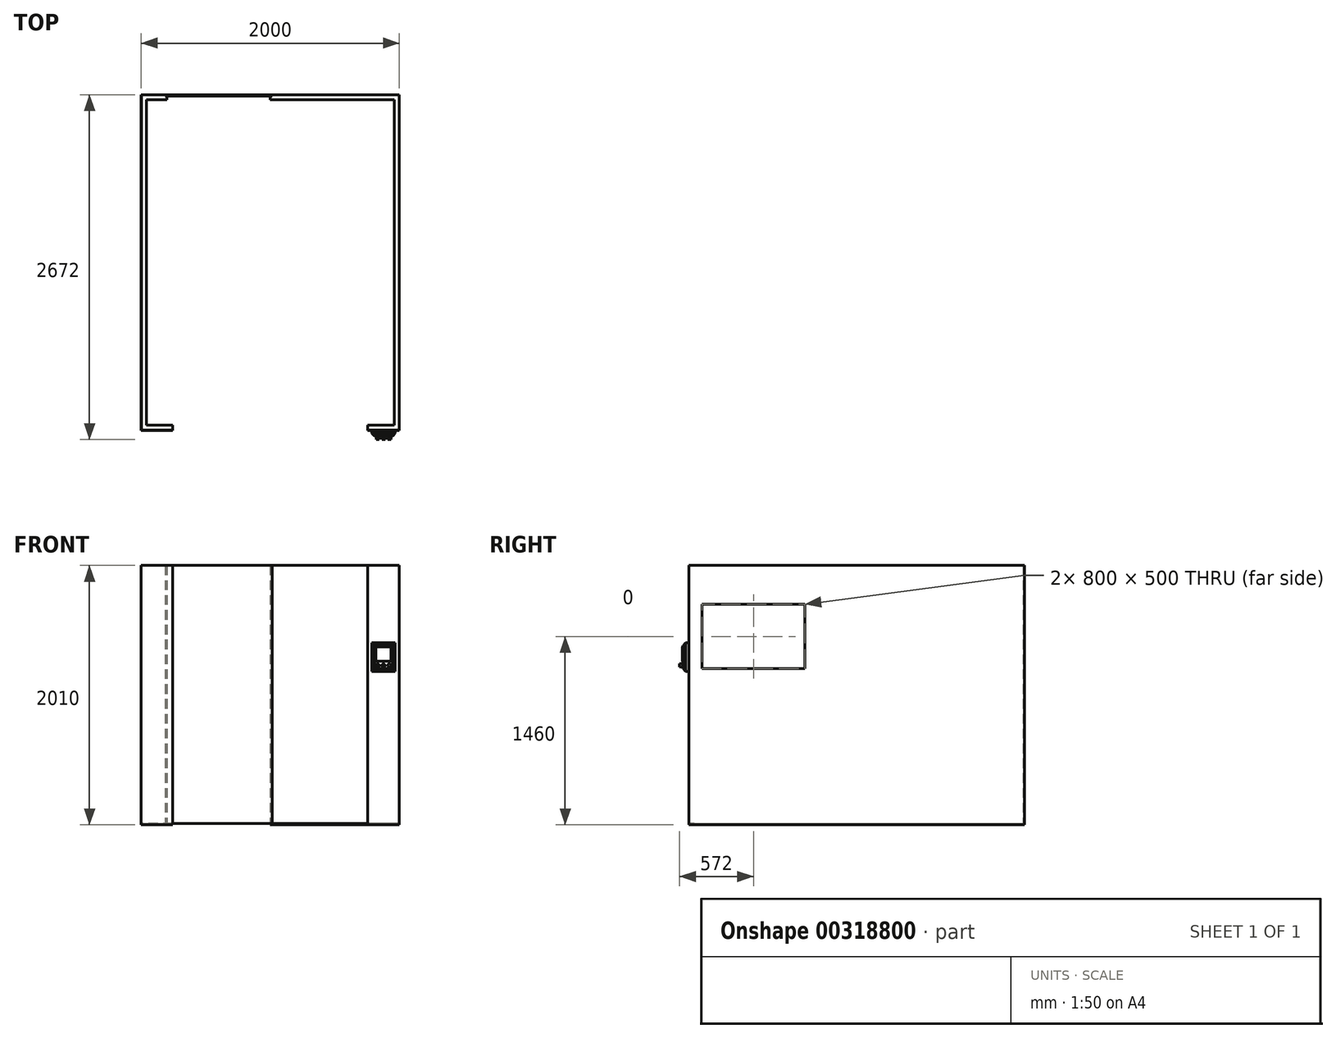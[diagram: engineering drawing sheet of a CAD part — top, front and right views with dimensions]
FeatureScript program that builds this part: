
annotation { "Feature Type Name" : "Feature", "Feature Type Description" : "" }
export const myFeature = defineFeature(function(context is Context, id is Id, definition is map)
    precondition{}
    {
        {
            var Q0;
            Q0=qCreatedBy(makeId("Top.planeOp"),FACE);
            var sketch = newSketch(context, id + "F0", { "sketchPlane" : qUnion([Q0])});
            skLineSegment(sketch, "E0", {"start": v(0, 0) * mm, "end": v(-755, 0) * mm, "construction": true});
            skLineSegment(sketch, "E1.MirrorCS", {"start": v(0, 0) * mm, "end": v(755, 0) * mm, "construction": true});
            skLineSegment(sketch, "E2", {"start": v(-755, 0) * mm, "end": v(-755, -20) * mm});
            skLineSegment(sketch, "E3", {"start": v(-755, -20) * mm, "end": v(-1000, -20) * mm});
            skLineSegment(sketch, "E4", {"start": v(-1000, -20) * mm, "end": v(-1000, 0) * mm});
            skLineSegment(sketch, "E5.MirrorCS", {"start": v(-755, 0) * mm, "end": v(-755, 20) * mm});
            skLineSegment(sketch, "E6.MirrorCS", {"start": v(-1000, 20) * mm, "end": v(-1000, 0) * mm});
            skLineSegment(sketch, "E7.MirrorCS", {"start": v(-755, 20) * mm, "end": v(-960, 20) * mm});
            skLineSegment(sketch, "E8.MirrorCS", {"start": v(755, 0) * mm, "end": v(755, -20) * mm});
            skLineSegment(sketch, "E9.MirrorCS", {"start": v(755, 0) * mm, "end": v(755, 20) * mm});
            skLineSegment(sketch, "E10.MirrorCS", {"start": v(1000, 20) * mm, "end": v(1000, 0) * mm});
            skLineSegment(sketch, "E11.MirrorCS", {"start": v(1000, -20) * mm, "end": v(1000, 0) * mm});
            skLineSegment(sketch, "E12.MirrorCS", {"start": v(755, 20) * mm, "end": v(960, 20) * mm});
            skLineSegment(sketch, "E13.MirrorCS", {"start": v(755, -20) * mm, "end": v(1000, -20) * mm});
            skLineSegment(sketch, "E14.left", {"start": v(-1000, 20) * mm, "end": v(-1000, 2540) * mm});
            skLineSegment(sketch, "E14.right", {"start": v(-960, 20) * mm, "end": v(-960, 2540) * mm});
            skLineSegment(sketch, "E15.MirrorCS", {"start": v(1000, 20) * mm, "end": v(1000, 2540) * mm});
            skLineSegment(sketch, "E16.MirrorCS", {"start": v(960, 20) * mm, "end": v(960, 2540) * mm});
            skLineSegment(sketch, "E17.bottom", {"start": v(-960, 2540) * mm, "end": v(-800, 2540) * mm});
            skLineSegment(sketch, "E17.top", {"start": v(-1000, 2580) * mm, "end": v(-800, 2580) * mm});
            skLineSegment(sketch, "E17.left", {"start": v(-1000, 2540) * mm, "end": v(-1000, 2580) * mm});
            skLineSegment(sketch, "E17.right", {"start": v(-800, 2540) * mm, "end": v(-800, 2580) * mm});
            skLineSegment(sketch, "E18.bottom", {"start": v(960, 2540) * mm, "end": v(0, 2540) * mm});
            skLineSegment(sketch, "E18.top", {"start": v(1000, 2580) * mm, "end": v(0, 2580) * mm});
            skLineSegment(sketch, "E18.left", {"start": v(1000, 2540) * mm, "end": v(1000, 2580) * mm});
            skLineSegment(sketch, "E18.right", {"start": v(0, 2540) * mm, "end": v(0, 2580) * mm});
            skSolve(sketch);
        }
        {
            var Q0;
            Q0=qSketchRegion(id+"F0",true);
            extrude(context, id + "F1", {"entities" : qUnion([Q0]), "depth" : 10 * mm});
        }
        {
            var Q0;
            Q0=makeQuery(id+"F1.opExtrude","CAP_FACE",FACE,{"disambiguationData":[OSD([sQuery(id+"F0.wireOp",EDGE,"E2"),sQuery(id+"F0.wireOp",EDGE,"E3"),sQuery(id+"F0.wireOp",EDGE,"E4"),sQuery(id+"F0.wireOp",EDGE,"E5.MirrorCS"),sQuery(id+"F0.wireOp",EDGE,"E6.MirrorCS"),sQuery(id+"F0.wireOp",EDGE,"E7.MirrorCS"),sQuery(id+"F0.wireOp",EDGE,"E14.left"),sQuery(id+"F0.wireOp",EDGE,"E14.right"),sQuery(id+"F0.wireOp",EDGE,"E17.bottom"),sQuery(id+"F0.wireOp",EDGE,"E17.top"),sQuery(id+"F0.wireOp",EDGE,"E17.left"),sQuery(id+"F0.wireOp",EDGE,"E17.right")])],"isStart":false});
            var sketch = newSketch(context, id + "F2", { "sketchPlane" : qUnion([Q0])});
            skLineSegment(sketch, "E19", {"start": v(-800, 2580) * mm, "end": v(-1000, 2580) * mm});
            skLineSegment(sketch, "E20", {"start": v(-1000, 2580) * mm, "end": v(-1000, -20) * mm});
            skLineSegment(sketch, "E21", {"start": v(-1000, -20) * mm, "end": v(-755, -20) * mm});
            skLineSegment(sketch, "E22", {"start": v(-755, -20) * mm, "end": v(-755, -18) * mm});
            skLineSegment(sketch, "E23", {"start": v(-755, -18) * mm, "end": v(-998, -18) * mm});
            skLineSegment(sketch, "E24", {"start": v(-998, -18) * mm, "end": v(-998, 2578) * mm});
            skLineSegment(sketch, "E25", {"start": v(-998, 2578) * mm, "end": v(-800, 2578) * mm});
            skLineSegment(sketch, "E26", {"start": v(-800, 2578) * mm, "end": v(-800, 2580) * mm});
            skSolve(sketch);
        }
        {
            var Q0;
            Q0=qSketchRegion(id+"F2",true);
            extrude(context, id + "F3", {"entities" : qUnion([Q0]), "operationType" : NewBodyOperationType.ADD, "depth" : 2000 * mm});
        }
        {
            var Q0;
            Q0=makeQuery(id+"F1.opExtrude","CAP_FACE",FACE,{"disambiguationData":[OSD([sQuery(id+"F0.wireOp",EDGE,"E8.MirrorCS"),sQuery(id+"F0.wireOp",EDGE,"E9.MirrorCS"),sQuery(id+"F0.wireOp",EDGE,"E11.MirrorCS"),sQuery(id+"F0.wireOp",EDGE,"E12.MirrorCS"),sQuery(id+"F0.wireOp",EDGE,"E13.MirrorCS"),sQuery(id+"F0.wireOp",EDGE,"E10.MirrorCS"),sQuery(id+"F0.wireOp",EDGE,"E15.MirrorCS"),sQuery(id+"F0.wireOp",EDGE,"E16.MirrorCS"),sQuery(id+"F0.wireOp",EDGE,"E18.bottom"),sQuery(id+"F0.wireOp",EDGE,"E18.top"),sQuery(id+"F0.wireOp",EDGE,"E18.left"),sQuery(id+"F0.wireOp",EDGE,"E18.right")])],"isStart":false});
            var sketch = newSketch(context, id + "F4", { "sketchPlane" : qUnion([Q0])});
            skLineSegment(sketch, "E27", {"start": v(0, 2580) * mm, "end": v(1000, 2580) * mm});
            skLineSegment(sketch, "E28", {"start": v(1000, 2580) * mm, "end": v(1000, -20) * mm});
            skLineSegment(sketch, "E29", {"start": v(1000, -20) * mm, "end": v(755, -20) * mm});
            skLineSegment(sketch, "E30", {"start": v(755, -20) * mm, "end": v(755, -18) * mm});
            skLineSegment(sketch, "E31", {"start": v(755, -18) * mm, "end": v(998, -18) * mm});
            skLineSegment(sketch, "E32", {"start": v(998, -18) * mm, "end": v(998, 2578) * mm});
            skLineSegment(sketch, "E33", {"start": v(998, 2578) * mm, "end": v(0, 2578) * mm});
            skLineSegment(sketch, "E34", {"start": v(0, 2578) * mm, "end": v(0, 2580) * mm});
            skSolve(sketch);
        }
        {
            var Q0;
            Q0=qSketchRegion(id+"F4",true);
            extrude(context, id + "F5", {"entities" : qUnion([Q0]), "operationType" : NewBodyOperationType.ADD, "depth" : 2000 * mm});
        }
        {
            var Q0;
            Q0=makeQuery(id+"F5.boolean.opBoolean","MERGE",FACE,{"derivedFrom":[makeQuery(id+"F1.opExtrude","SWEPT_FACE",FACE,{"disambiguationData":[OSD([sQuery(id+"F0.wireOp",EDGE,"E18.top")])]}),makeQuery(id+"F5.opExtrude","SWEPT_FACE",FACE,{"disambiguationData":[OSD([sQuery(id+"F4.wireOp",EDGE,"E27")])]})]});
            var sketch = newSketch(context, id + "F6", { "sketchPlane" : qUnion([Q0])});
            skLineSegment(sketch, "E35.bottom", {"start": v(-15, 2010) * mm, "end": v(815, 2010) * mm});
            skLineSegment(sketch, "E35.top", {"start": v(-15, 10) * mm, "end": v(815, 10) * mm});
            skLineSegment(sketch, "E35.left", {"start": v(-15, 2010) * mm, "end": v(-15, 10) * mm});
            skLineSegment(sketch, "E35.right", {"start": v(815, 2010) * mm, "end": v(815, 10) * mm});
            skSolve(sketch);
        }
        {
            var Q0;
            Q0=qSketchRegion(id+"F6",true);
            extrude(context, id + "F7", {"entities" : qUnion([Q0]), "oppositeDirection" : true, "depth" : 10 * mm});
        }
        {
            var Q0;
            Q0=makeQuery(id+"F5.boolean.opBoolean","MERGE",FACE,{"derivedFrom":[makeQuery(id+"F1.opExtrude","SWEPT_FACE",FACE,{"disambiguationData":[OSD([sQuery(id+"F0.wireOp",EDGE,"E11.MirrorCS"),sQuery(id+"F0.wireOp",EDGE,"E10.MirrorCS"),sQuery(id+"F0.wireOp",EDGE,"E15.MirrorCS"),sQuery(id+"F0.wireOp",EDGE,"E18.left")])]}),makeQuery(id+"F5.opExtrude","SWEPT_FACE",FACE,{"disambiguationData":[OSD([sQuery(id+"F4.wireOp",EDGE,"E28")])]})]});
            var sketch = newSketch(context, id + "F8", { "sketchPlane" : qUnion([Q0])});
            skLineSegment(sketch, "E36.bottom", {"start": v(80, 1710) * mm, "end": v(880, 1710) * mm});
            skLineSegment(sketch, "E36.top", {"start": v(80, 1210) * mm, "end": v(880, 1210) * mm});
            skLineSegment(sketch, "E36.left", {"start": v(80, 1710) * mm, "end": v(80, 1210) * mm});
            skLineSegment(sketch, "E36.right", {"start": v(880, 1710) * mm, "end": v(880, 1210) * mm});
            skSolve(sketch);
        }
        {
            var Q0;
            Q0=qSketchRegion(id+"F8",true);
            extrude(context, id + "F9", {"entities" : qUnion([Q0]), "operationType" : NewBodyOperationType.REMOVE, "oppositeDirection" : true, "depth" : 5 * mm});
        }
        {
            var Q0;
            Q0=makeQuery(id+"F3.boolean.opBoolean","MERGE",FACE,{"derivedFrom":[makeQuery(id+"F1.opExtrude","SWEPT_FACE",FACE,{"disambiguationData":[OSD([sQuery(id+"F0.wireOp",EDGE,"E4"),sQuery(id+"F0.wireOp",EDGE,"E6.MirrorCS"),sQuery(id+"F0.wireOp",EDGE,"E14.left"),sQuery(id+"F0.wireOp",EDGE,"E17.left")])]}),makeQuery(id+"F3.opExtrude","SWEPT_FACE",FACE,{"disambiguationData":[OSD([sQuery(id+"F2.wireOp",EDGE,"E20")])]})]});
            var sketch = newSketch(context, id + "F10", { "sketchPlane" : qUnion([Q0])});
            skLineSegment(sketch, "E37.bottom", {"start": v(-880, 1710) * mm, "end": v(-80, 1710) * mm});
            skLineSegment(sketch, "E37.top", {"start": v(-880, 1210) * mm, "end": v(-80, 1210) * mm});
            skLineSegment(sketch, "E37.left", {"start": v(-880, 1710) * mm, "end": v(-880, 1210) * mm});
            skLineSegment(sketch, "E37.right", {"start": v(-80, 1710) * mm, "end": v(-80, 1210) * mm});
            skSolve(sketch);
        }
        {
            var Q0;
            Q0=qSketchRegion(id+"F10",true);
            extrude(context, id + "F11", {"entities" : qUnion([Q0]), "operationType" : NewBodyOperationType.REMOVE, "oppositeDirection" : true, "depth" : 5 * mm});
        }
        {
            var Q0;
            Q0=makeQuery(id+"F3.boolean.opBoolean","MERGE",FACE,{"derivedFrom":[makeQuery(id+"F1.opExtrude","SWEPT_FACE",FACE,{"disambiguationData":[OSD([sQuery(id+"F0.wireOp",EDGE,"E4"),sQuery(id+"F0.wireOp",EDGE,"E6.MirrorCS"),sQuery(id+"F0.wireOp",EDGE,"E14.left"),sQuery(id+"F0.wireOp",EDGE,"E17.left")])]}),makeQuery(id+"F3.opExtrude","SWEPT_FACE",FACE,{"disambiguationData":[OSD([sQuery(id+"F2.wireOp",EDGE,"E20")])]})]});
            var sketch = newSketch(context, id + "F12", { "sketchPlane" : qUnion([Q0])});
            skLineSegment(sketch, "E38.bottom", {"start": v(-880, 1710) * mm, "end": v(-80, 1710) * mm});
            skLineSegment(sketch, "E38.top", {"start": v(-880, 1210) * mm, "end": v(-80, 1210) * mm});
            skLineSegment(sketch, "E38.left", {"start": v(-880, 1710) * mm, "end": v(-880, 1210) * mm});
            skLineSegment(sketch, "E38.right", {"start": v(-80, 1710) * mm, "end": v(-80, 1210) * mm});
            skSolve(sketch);
        }
        {
            var Q0;
            Q0=qSketchRegion(id+"F12",true);
            extrude(context, id + "F13", {"entities" : qUnion([Q0]), "oppositeDirection" : true, "depth" : 2 * mm});
        }
        {
            var Q0;
            Q0=makeQuery(id+"F5.boolean.opBoolean","MERGE",FACE,{"derivedFrom":[makeQuery(id+"F1.opExtrude","SWEPT_FACE",FACE,{"disambiguationData":[OSD([sQuery(id+"F0.wireOp",EDGE,"E11.MirrorCS"),sQuery(id+"F0.wireOp",EDGE,"E10.MirrorCS"),sQuery(id+"F0.wireOp",EDGE,"E15.MirrorCS"),sQuery(id+"F0.wireOp",EDGE,"E18.left")])]}),makeQuery(id+"F5.opExtrude","SWEPT_FACE",FACE,{"disambiguationData":[OSD([sQuery(id+"F4.wireOp",EDGE,"E28")])]})]});
            var sketch = newSketch(context, id + "F14", { "sketchPlane" : qUnion([Q0])});
            skLineSegment(sketch, "E39.bottom", {"start": v(80, 1710) * mm, "end": v(880, 1710) * mm});
            skLineSegment(sketch, "E39.top", {"start": v(80, 1210) * mm, "end": v(880, 1210) * mm});
            skLineSegment(sketch, "E39.left", {"start": v(80, 1710) * mm, "end": v(80, 1210) * mm});
            skLineSegment(sketch, "E39.right", {"start": v(880, 1710) * mm, "end": v(880, 1210) * mm});
            skSolve(sketch);
        }
        {
            var Q0;
            Q0=qSketchRegion(id+"F14",true);
            extrude(context, id + "F15", {"entities" : qUnion([Q0]), "oppositeDirection" : true, "depth" : 2 * mm});
        }
        {
            var Q0;
            Q0=makeQuery(id+"F3.opExtrude","SWEPT_FACE",FACE,{"disambiguationData":[OSD([sQuery(id+"F2.wireOp",EDGE,"E25")])]});
            var sketch = newSketch(context, id + "F16", { "sketchPlane" : qUnion([Q0])});
            skLineSegment(sketch, "E40", {"start": v(-800, 10) * mm, "end": v(-815, 10) * mm});
            skPoint(sketch, "E41", {"position": v(-815, 10) * mm});
            skSolve(sketch);
        }
        {
            var Q0;
            Q0=makeQuery(id+"F5.boolean.opBoolean","MERGE",FACE,{"derivedFrom":[makeQuery(id+"F1.opExtrude","SWEPT_FACE",FACE,{"disambiguationData":[OSD([sQuery(id+"F0.wireOp",EDGE,"E13.MirrorCS")])]}),makeQuery(id+"F5.opExtrude","SWEPT_FACE",FACE,{"disambiguationData":[OSD([sQuery(id+"F4.wireOp",EDGE,"E29")])]})]});
            var sketch = newSketch(context, id + "F17", { "sketchPlane" : qUnion([Q0])});
            skLineSegment(sketch, "E42.bottom", {"start": v(787.5, 1410) * mm, "end": v(967.5, 1410) * mm});
            skLineSegment(sketch, "E42.top", {"start": v(787.5, 1190) * mm, "end": v(967.5, 1190) * mm});
            skLineSegment(sketch, "E42.left", {"start": v(787.5, 1410) * mm, "end": v(787.5, 1190) * mm});
            skLineSegment(sketch, "E42.right", {"start": v(967.5, 1410) * mm, "end": v(967.5, 1190) * mm});
            skSolve(sketch);
        }
        {
            var Q0;
            Q0=qSketchRegion(id+"F17",true);
            extrude(context, id + "F18", {"entities" : qUnion([Q0]), "depth" : 25 * mm});
        }
        {
            var Q0;
            Q0=makeQuery(id+"F18.opExtrude","CAP_FACE",FACE,{"disambiguationData":[OSD([sQuery(id+"F17.wireOp",EDGE,"E42.bottom"),sQuery(id+"F17.wireOp",EDGE,"E42.top"),sQuery(id+"F17.wireOp",EDGE,"E42.left"),sQuery(id+"F17.wireOp",EDGE,"E42.right")])],"isStart":false});
            cPlane(context, id + "F19", {"entities" : qUnion([Q0]), "cplaneType" : CPlaneType.OFFSET, "offset" : 20 * mm, "width" : 150 * mm, "height" : 150 * mm});
        }
        {
            var Q0;
            Q0=qCreatedBy(id+"F19.planeOp",FACE);
            var sketch = newSketch(context, id + "F20", { "sketchPlane" : qUnion([Q0])});
            skLineSegment(sketch, "E43.0", {"start": v(947.5, 1390) * mm, "end": v(947.5, 1210) * mm});
            skLineSegment(sketch, "E44.0", {"start": v(807.5, 1390) * mm, "end": v(947.5, 1390) * mm});
            skLineSegment(sketch, "E45.0", {"start": v(807.5, 1390) * mm, "end": v(807.5, 1210) * mm});
            skLineSegment(sketch, "E46.0", {"start": v(807.5, 1210) * mm, "end": v(947.5, 1210) * mm});
            skPoint(sketch, "E47.orphan", {"position": v(787.5, 1410) * mm});
            skPoint(sketch, "E48.orphan", {"position": v(787.5, 1190) * mm});
            skPoint(sketch, "E49.0.end.orphan", {"position": v(967.5, 1190) * mm});
            skPoint(sketch, "E50.0.start.orphan", {"position": v(967.5, 1410) * mm});
            skSolve(sketch);
        }
        {
            var Q0;
            Q0=makeQuery(id+"F18.opExtrude","CAP_FACE",FACE,{"disambiguationData":[OSD([sQuery(id+"F17.wireOp",EDGE,"E42.bottom"),sQuery(id+"F17.wireOp",EDGE,"E42.top"),sQuery(id+"F17.wireOp",EDGE,"E42.left"),sQuery(id+"F17.wireOp",EDGE,"E42.right")])],"isStart":false});
            var Q1;
            Q1=makeQuery(id+"F20.imprint","IMPRINT",FACE,{"disambiguationData":[TD([[makeQuery(id+"F20.imprint","IMPRINT",EDGE,{"derivedFrom":sQuery(id+"F20.wireOp",EDGE,"E43.0")}),-1.0]])]});
            var Q2;
            Q2=sQuery(id+"F20.wireOp",EDGE,"E46.0");
            var Q3;
            Q3=sQuery(id+"F20.wireOp",EDGE,"E45.0");
            var Q4;
            Q4=sQuery(id+"F20.wireOp",EDGE,"E44.0");
            var Q5;
            Q5=sQuery(id+"F20.wireOp",EDGE,"E43.0");
            loft(context, id + "F21", {"sheetProfilesArray" : [{ "sheetProfileEntities" : qUnion([Q0]) }, { "sheetProfileEntities" : qUnion([Q1]) }], "guidesArray" : [{ "guideEntities" : qUnion([Q2]), "guideDerivativeType" : LoftGuideDerivativeType.DEFAULT, "guideDerivativeMagnitude" : 1 }, { "guideEntities" : qUnion([Q3]), "guideDerivativeType" : LoftGuideDerivativeType.DEFAULT, "guideDerivativeMagnitude" : 1 }, { "guideEntities" : qUnion([Q4]), "guideDerivativeType" : LoftGuideDerivativeType.DEFAULT, "guideDerivativeMagnitude" : 1 }, { "guideEntities" : qUnion([Q5]), "guideDerivativeType" : LoftGuideDerivativeType.DEFAULT, "guideDerivativeMagnitude" : 1 }]});
        }
        {
            var Q0;
            Q0=makeQuery(id+"F21.opLoft","CAP_FACE",FACE,{"disambiguationData":[OSD([makeQuery(id+"F20.imprint","IMPRINT",FACE,{"disambiguationData":[TD([[makeQuery(id+"F20.imprint","IMPRINT",EDGE,{"derivedFrom":sQuery(id+"F20.wireOp",EDGE,"E43.0")}),-1.0]])]})])],"isStart":true});
            extrude(context, id + "F22", {"entities" : qUnion([Q0]), "endBound" : BoundingType.SYMMETRIC, "depth" : 4 * mm});
        }
        {
            var Q0;
            Q0=makeQuery(id+"F22.opExtrude","CAP_FACE",FACE,{"disambiguationData":[OSD([makeQuery(id+"F20.imprint","IMPRINT",FACE,{"disambiguationData":[TD([[makeQuery(id+"F20.imprint","IMPRINT",EDGE,{"derivedFrom":sQuery(id+"F20.wireOp",EDGE,"E43.0")}),-1.0]])]})])],"isStart":false});
            var sketch = newSketch(context, id + "F23", { "sketchPlane" : qUnion([Q0])});
            skCircle(sketch, "E51", {"center": v(877.5, 1235) * mm, "radius": 12.5 * mm});
            skPoint(sketch, "E51.centerSnap0", {"position": v(877.5, 1210) * mm});
            skCircle(sketch, "E52", {"center": v(832.5, 1235) * mm, "radius": 12.5 * mm});
            skCircle(sketch, "E53", {"center": v(922.5, 1235) * mm, "radius": 12.5 * mm});
            skLineSegment(sketch, "E54", {"start": v(877.5, 1235) * mm, "end": v(832.5, 1235) * mm, "construction": true});
            skLineSegment(sketch, "E55", {"start": v(877.5, 1235) * mm, "end": v(922.5, 1235) * mm, "construction": true});
            skSolve(sketch);
        }
        {
            var Q0;
            Q0=qSketchRegion(id+"F23",true);
            extrude(context, id + "F24", {"entities" : qUnion([Q0]), "depth" : 25 * mm});
        }
        {
            var Q0;
            Q0=makeQuery(id+"F22.opExtrude","CAP_FACE",FACE,{"disambiguationData":[OSD([makeQuery(id+"F20.imprint","IMPRINT",FACE,{"disambiguationData":[TD([[makeQuery(id+"F20.imprint","IMPRINT",EDGE,{"derivedFrom":sQuery(id+"F20.wireOp",EDGE,"E43.0")}),-1.0]])]})])],"isStart":false});
            var sketch = newSketch(context, id + "F25", { "sketchPlane" : qUnion([Q0])});
            skLineSegment(sketch, "E56.bottom", {"start": v(935.5, 1378) * mm, "end": v(819.5, 1378) * mm});
            skLineSegment(sketch, "E56.top", {"start": v(935.5, 1268) * mm, "end": v(819.5, 1268) * mm});
            skLineSegment(sketch, "E56.left", {"start": v(935.5, 1378) * mm, "end": v(935.5, 1268) * mm});
            skLineSegment(sketch, "E56.right", {"start": v(819.5, 1378) * mm, "end": v(819.5, 1268) * mm});
            skSolve(sketch);
        }
        {
            var Q0;
            Q0=qSketchRegion(id+"F25",true);
            var Q1;
            Q1=makeQuery(id+"F25.imprint","IMPRINT",FACE,{"disambiguationData":[TD([[makeQuery(id+"F25.imprint","IMPRINT",EDGE,{"derivedFrom":sQuery(id+"F25.wireOp",EDGE,"E56.bottom")}),1.0]])]});
            extrude(context, id + "F26", {"entities" : qUnion([Q0, Q1]), "depth" : 3 * mm});
        }
    });
